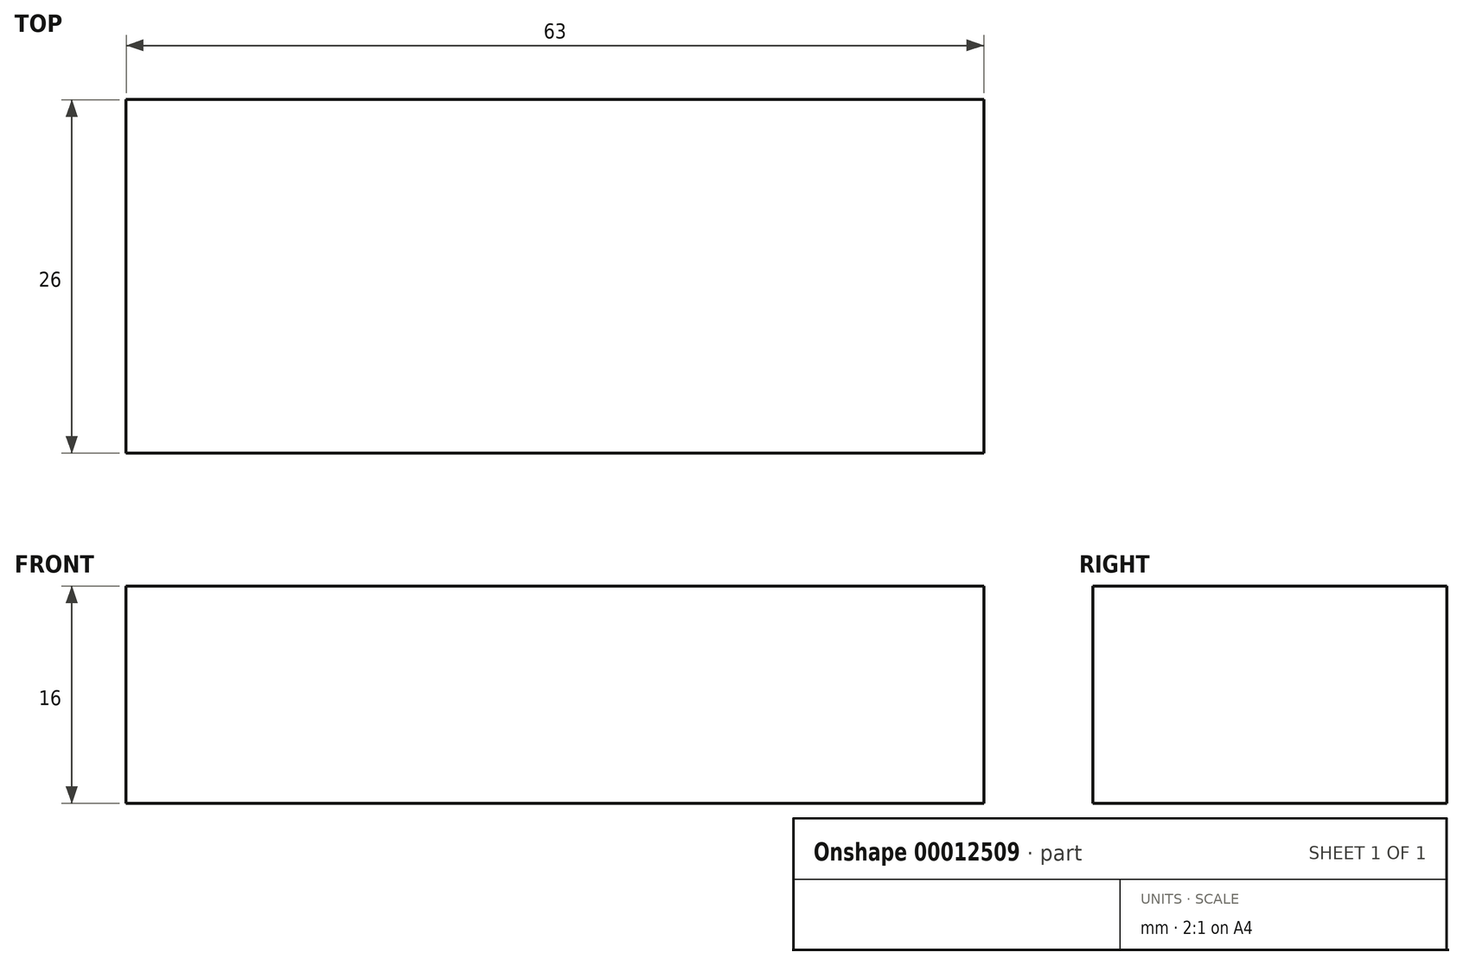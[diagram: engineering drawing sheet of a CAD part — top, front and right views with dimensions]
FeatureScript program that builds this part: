
annotation { "Feature Type Name" : "Feature", "Feature Type Description" : "" }
export const myFeature = defineFeature(function(context is Context, id is Id, definition is map)
    precondition{}
    {
        {
            var Q0;
            Q0=qCreatedBy(makeId("Top.planeOp"),FACE);
            var sketch = newSketch(context, id + "F0", { "sketchPlane" : qUnion([Q0])});
            skLineSegment(sketch, "E0.bottom", {"start": v(-85.72, 2.28) * mm, "end": v(-22.72, 2.28) * mm});
            skLineSegment(sketch, "E0.top", {"start": v(-85.72, -23.72) * mm, "end": v(-22.72, -23.72) * mm});
            skLineSegment(sketch, "E0.left", {"start": v(-85.72, 2.28) * mm, "end": v(-85.72, -23.72) * mm});
            skLineSegment(sketch, "E0.right", {"start": v(-22.72, 2.28) * mm, "end": v(-22.72, -23.72) * mm});
            skSolve(sketch);
        }
        {
            var Q0;
            Q0=makeQuery(id+"F0.imprint","IMPRINT",FACE,{"disambiguationData":[TD([[makeQuery(id+"F0.imprint","IMPRINT",EDGE,{"derivedFrom":sQuery(id+"F0.wireOp",EDGE,"E0.bottom")}),-1.0]])]});
            extrude(context, id + "F1", {"entities" : qUnion([Q0]), "depth" : 16 * mm});
        }
    });
